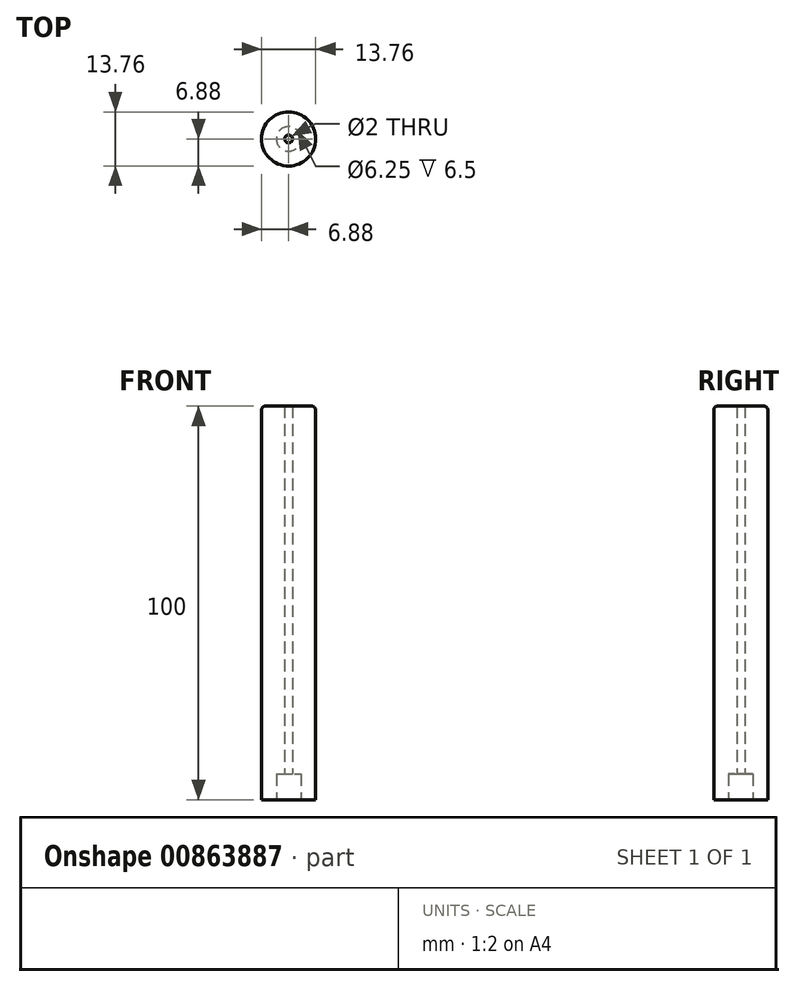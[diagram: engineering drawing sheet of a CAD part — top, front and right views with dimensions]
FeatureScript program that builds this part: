
annotation { "Feature Type Name" : "Feature", "Feature Type Description" : "" }
export const myFeature = defineFeature(function(context is Context, id is Id, definition is map)
    precondition{}
    {
        {
            var Q0;
            Q0=qCreatedBy(makeId("Top.planeOp"),FACE);
            var sketch = newSketch(context, id + "F0", { "sketchPlane" : qUnion([Q0])});
            skCircle(sketch, "E0", {"center": v(0, 0) * mm, "radius": 6.87 * mm});
            skSolve(sketch);
        }
        {
            var Q0;
            Q0 = qSketchRegion(id + "F0", true);
            extrude(context, id + "F1", {"entities" : qUnion([Q0]), "depth" : 100 * mm, "offsetDistance" : 25 * mm});
        }
        {
            var Q0;
            Q0=makeQuery(id+"F1.opExtrude","CAP_FACE",FACE,{"disambiguationData":[OSD([sQuery(id+"F0.wireOp",EDGE,"E0")])],"isStart":true});
            var sketch = newSketch(context, id + "F2", { "sketchPlane" : qUnion([Q0])});
            skPoint(sketch, "E1", {"position": v(0, 0) * mm});
            skSolve(sketch);
        }
        {
            var Q0;
            Q0=sQuery(id+"F2.wireOp",VERTEX,"E1");
            var Q1;
            Q1=makeQuery(id+"F1.opExtrude","SWEPT_BODY",BODY,{"disambiguationData":[OSD([sQuery(id+"F0.wireOp",EDGE,"E0")])]});
            hole(context, id + "F3", {"style" : HoleStyle.C_BORE, "endStyle" : HoleEndStyle.THROUGH, "holeDiameter" : 2 * mm, "cBoreDiameter" : 6.25 * mm, "cBoreDepth" : 6.5 * mm, "majorDiameter" : 5 * mm, "isTappedThrough" : true, "tappedDepth" : 12 * mm, "tapClearance" : 3, "startFromSketch" : true, "locations" : qUnion([Q0]), "scope" : qUnion([Q1])});
        }
        {
            var Q0;
            Q0=makeQuery(id+"F1.opExtrude","CAP_EDGE",EDGE,{"disambiguationData":[OSD([sQuery(id+"F0.wireOp",EDGE,"E0")])],"isStart":false});
            fillet(context, id + "F4", {"entities" : qUnion([Q0]), "radius" : 1 * mm, "tangentPropagation" : true, "allowEdgeOverflow" : false});
        }
    });
